# Revit family: SNS GDP2X
name_source: partatom
category: Electrical Equipment
units: mm (PartAtom-declared; Revit-internal decimal feet)

## family parameters
Always vertical = Yes
Cut with Voids When Loaded = No
OmniClass Number = 23.80.30.11.17
OmniClass Title = Distribution Boards and Control Panels
Part Type = Other Panel
Room Calculation Point = No
Round Connector Dimension = Use Diameter
Shared = No
Work Plane-Based = No

## types (1)
- SNS GDP2X
    Default Height = 4' - 0"
    Description = The Merlin GDP2X is an 8 zone gas detection panel which can be used in many applications, e.g. mechanical rooms, car parks, shopping malls and the most common being a boiler house application.

The GDP2X has a touch screen which displays two modes, the engineers mode and the user mode. A settings dip switch inside the controller allows the engineer/user to configure the system. When changes have been, the system will automatically restart once the settings switch is off.
    Load = 120 VA
    Manufacturer = S&S Northern Ltd.
    Model = SNS GDP2X
    Product Information = https://snsnorthern.com
    Type Comments = The Merlin GDP2X is an 8 zone gas detection panel which can be used in many applications, e.g. mechanical rooms, car parks, shopping malls and the most common being a boiler house application.

The GDP2X has a touch screen which displays two modes, the engineers mode and the user mode. A settings dip switch inside the controller allows the engineer/user to configure the system. When changes have been, the system will automatically restart once the settings switch is off.
    URL = https://snsnorthern.com
    Voltage = 120VAC

## geometry (parser evidence)
native form markers: Sweep x14
no freeform markers — native parametric forms only
